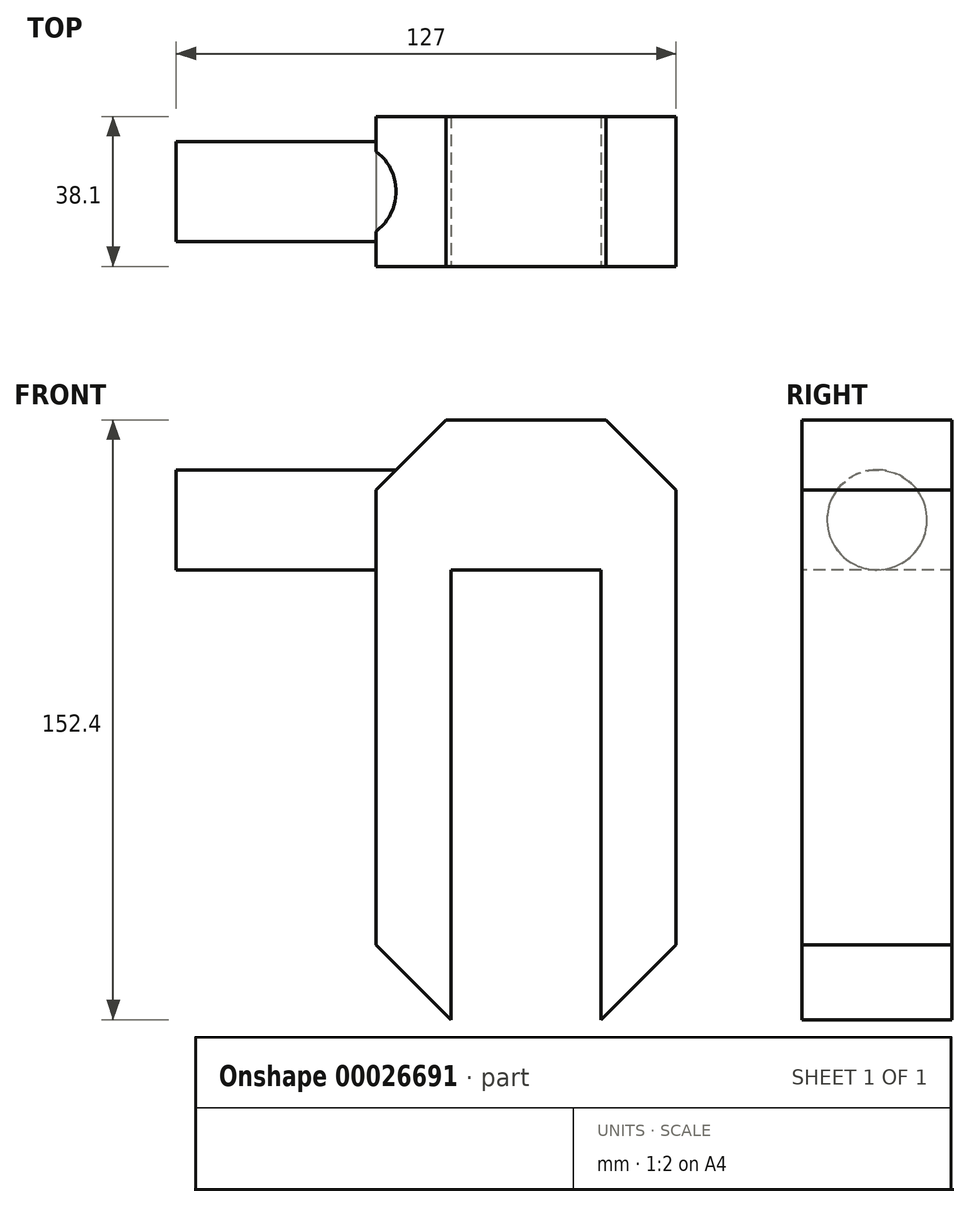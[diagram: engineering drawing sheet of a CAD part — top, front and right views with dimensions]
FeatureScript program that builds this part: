
annotation { "Feature Type Name" : "Feature", "Feature Type Description" : "" }
export const myFeature = defineFeature(function(context is Context, id is Id, definition is map)
    precondition{}
    {
        {
            var Q0;
            Q0=qCreatedBy(makeId("Front.planeOp"),FACE);
            var sketch = newSketch(context, id + "F0", { "sketchPlane" : qUnion([Q0])});
            skLineSegment(sketch, "E0.bottom", {"start": v(-28.31, 122.94) * mm, "end": v(47.89, 122.94) * mm});
            skLineSegment(sketch, "E0.top", {"start": v(-28.31, -29.46) * mm, "end": v(47.89, -29.46) * mm});
            skLineSegment(sketch, "E0.left", {"start": v(-28.31, 122.94) * mm, "end": v(-28.31, -29.46) * mm});
            skLineSegment(sketch, "E0.right", {"start": v(47.89, 122.94) * mm, "end": v(47.89, -29.46) * mm});
            skPoint(sketch, "E1.start.orphan", {"position": v(-28.31, 46.74) * mm});
            skSolve(sketch);
        }
        {
            var Q0;
            Q0=makeQuery(id+"F0.imprint","IMPRINT",FACE,{"disambiguationData":[TD([[makeQuery(id+"F0.imprint","IMPRINT",EDGE,{"derivedFrom":sQuery(id+"F0.wireOp",EDGE,"E0.bottom")}),-1.0]])]});
            extrude(context, id + "F1", {"entities" : qUnion([Q0]), "depth" : 38.1 * mm});
        }
        {
            var Q0;
            Q0=makeQuery(id+"F1.opExtrude","SWEPT_FACE",FACE,{"disambiguationData":[OSD([sQuery(id+"F0.wireOp",EDGE,"E0.left")])]});
            var sketch = newSketch(context, id + "F2", { "sketchPlane" : qUnion([Q0])});
            skCircle(sketch, "E2", {"center": v(19.05, 97.54) * mm, "radius": 12.7 * mm});
            skSolve(sketch);
        }
        {
            var Q0;
            Q0=makeQuery(id+"F2.imprint","IMPRINT",FACE,{"disambiguationData":[TD([[makeQuery(id+"F2.imprint","IMPRINT",EDGE,{"derivedFrom":sQuery(id+"F2.wireOp",EDGE,"E2")}),1.0]])]});
            extrude(context, id + "F3", {"entities" : qUnion([Q0]), "operationType" : NewBodyOperationType.ADD, "depth" : 50.8 * mm});
        }
        {
            var Q0;
            Q0=makeQuery(id+"F1.opExtrude","SWEPT_EDGE",EDGE,{"disambiguationData":[OSD([sQuery(id+"F0.wireOp",EDGE,"E0.bottom"),sQuery(id+"F0.wireOp",EDGE,"E0.right")])]});
            chamfer(context, id + "F4", {"entities" : qUnion([Q0]), "width" : 17.78 * mm, "tangentPropagation" : true});
        }
        {
            var Q0;
            Q0=makeQuery(id+"F1.opExtrude","SWEPT_EDGE",EDGE,{"disambiguationData":[OSD([sQuery(id+"F0.wireOp",EDGE,"E0.bottom"),sQuery(id+"F0.wireOp",EDGE,"E0.left")])]});
            chamfer(context, id + "F5", {"entities" : qUnion([Q0]), "width" : 17.78 * mm, "tangentPropagation" : true});
        }
        {
            var Q0;
            Q0=makeQuery(id+"F1.opExtrude","CAP_FACE",FACE,{"disambiguationData":[OSD([sQuery(id+"F0.wireOp",EDGE,"E0.bottom"),sQuery(id+"F0.wireOp",EDGE,"E0.top"),sQuery(id+"F0.wireOp",EDGE,"E0.left"),sQuery(id+"F0.wireOp",EDGE,"E0.right")])],"isStart":false});
            var sketch = newSketch(context, id + "F6", { "sketchPlane" : qUnion([Q0])});
            skPoint(sketch, "E3.start.orphan", {"position": v(0, -29.46) * mm});
            skLineSegment(sketch, "E4", {"start": v(-9.26, -29.46) * mm, "end": v(-9.26, 84.84) * mm});
            skLineSegment(sketch, "E5", {"start": v(-9.26, 84.84) * mm, "end": v(28.84, 84.84) * mm});
            skLineSegment(sketch, "E6", {"start": v(28.84, 84.84) * mm, "end": v(28.84, -29.46) * mm});
            skSolve(sketch);
        }
        {
            var Q0;
            {var subQ2=sQuery(id+"F6.wireOp",EDGE,"E4");Q0=makeQuery(id+"F6.imprint","IMPRINT",FACE,{"disambiguationData":[TD([[makeQuery(id+"F6.imprint","IMPRINT",EDGE,{"derivedFrom":subQ2}),-1.0]])]});}
            extrude(context, id + "F7", {"entities" : qUnion([Q0]), "operationType" : NewBodyOperationType.REMOVE, "endBound" : BoundingType.THROUGH_ALL, "oppositeDirection" : true, "depth" : 25.4 * mm});
        }
        {
            var Q0;
            Q0=makeQuery(id+"F1.opExtrude","SWEPT_EDGE",EDGE,{"disambiguationData":[OSD([sQuery(id+"F0.wireOp",EDGE,"E0.top"),sQuery(id+"F0.wireOp",EDGE,"E0.left")])]});
            chamfer(context, id + "F8", {"entities" : qUnion([Q0]), "width" : 19.05 * mm, "tangentPropagation" : true});
        }
        {
            var Q0;
            Q0=makeQuery(id+"F1.opExtrude","SWEPT_EDGE",EDGE,{"disambiguationData":[OSD([sQuery(id+"F0.wireOp",EDGE,"E0.top"),sQuery(id+"F0.wireOp",EDGE,"E0.right")])]});
            chamfer(context, id + "F9", {"entities" : qUnion([Q0]), "width" : 19.05 * mm, "tangentPropagation" : true});
        }
    });
